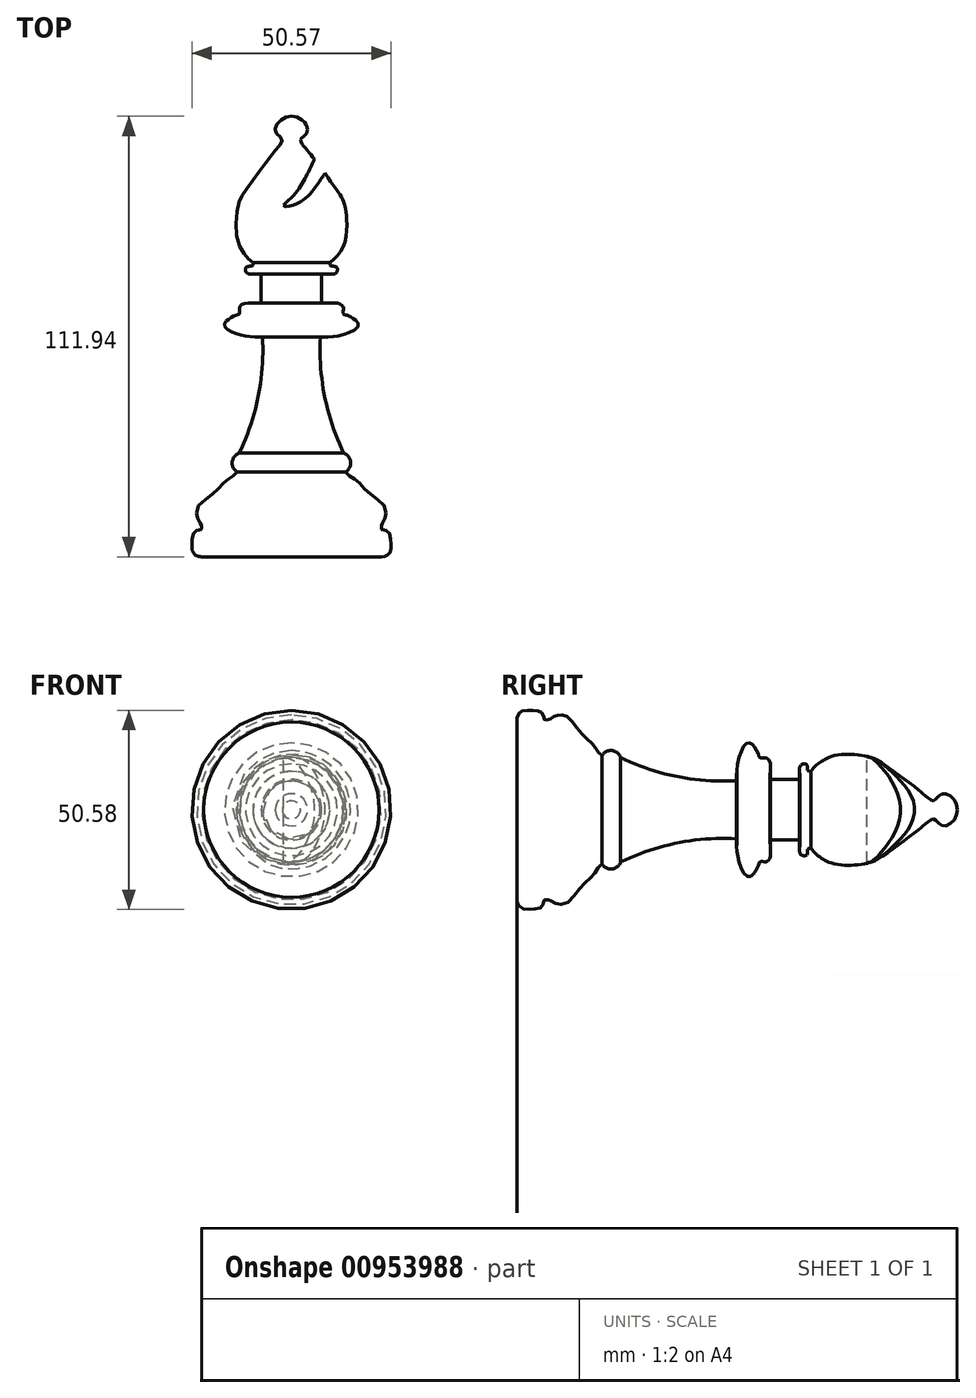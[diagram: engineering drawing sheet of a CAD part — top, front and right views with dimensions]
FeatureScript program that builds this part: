
annotation { "Feature Type Name" : "Feature", "Feature Type Description" : "" }
export const myFeature = defineFeature(function(context is Context, id is Id, definition is map)
    precondition{}
    {
        {
            var Q0;
            Q0=qCreatedBy(makeId("Top.planeOp"),FACE);
            var sketch = newSketch(context, id + "F0", { "sketchPlane" : qUnion([Q0])});
            skLineSegment(sketch, "E0", {"start": v(6.72, 66.6) * mm, "end": v(6.72, -45.31) * mm});
            skLineSegment(sketch, "E1", {"start": v(6.72, -45.31) * mm, "end": v(-15.55, -45.31) * mm});
            skFitSpline(sketch, "E2", {"points": [v(-15.55, -45.31) * mm, v(-16.6, -45.31) * mm, v(-18.04, -44.66) * mm, v(-18.53, -43.6) * mm, v(-18.53, -41.43) * mm, v(-18.4, -39.98) * mm, v(-17.92, -39.05) * mm, v(-16.91, -38.57) * mm, v(-16.19, -38.36) * mm, v(-16.1, -37.96) * mm, v(-16.19, -37.15) * mm, v(-16.75, -36.3) * mm, v(-17.12, -35.54) * mm, v(-17.32, -34.5) * mm, v(-17.16, -32.84) * mm, v(-14.45, -30.33) * mm, v(-11.67, -27.87) * mm, v(-9.7, -25.9) * mm, v(-8.08, -24.77) * mm, v(-7.07, -23.8) * mm], "startDerivative": vector(-21.72, -2.35) * mm, "endDerivative": vector(17.85, 19.31) * mm});
            skArc(sketch, "E3", {"start": v(-6.54, -19) * mm, "mid": v(-8.32, -21.23) * mm, "end": v(-7.07, -23.8) * mm});
            skArc(sketch, "E4", {"start": v(-6.54, -19) * mm, "mid": v(-1.72, -4.59) * mm, "end": v(-0.65, 10.57) * mm});
            skFitSpline(sketch, "E5", {"points": [v(-0.65, 10.57) * mm, v(-4.03, 10.57) * mm, v(-8.7, 11.9) * mm, v(-10.27, 13.25) * mm, v(-9.93, 14.4) * mm, v(-8.98, 15.15) * mm, v(-7.35, 16.04) * mm, v(-6.54, 16.3) * mm, v(-6.47, 17.32) * mm, v(-6.47, 18) * mm, v(-5.8, 18.82) * mm, v(-4.1, 19.09) * mm, v(-2.47, 18.95) * mm, v(-1.38, 18.96) * mm, v(-0.98, 19.04) * mm], "startDerivative": vector(-29.3, -2.17) * mm, "endDerivative": vector(9.52, 2.58) * mm});
            skLineSegment(sketch, "E6", {"start": v(-0.98, 19.04) * mm, "end": v(-0.98, 26.49) * mm});
            skFitSpline(sketch, "E7", {"points": [v(-0.98, 26.49) * mm, v(-2.7, 26.49) * mm, v(-4.03, 26.49) * mm, v(-4.7, 26.83) * mm, v(-4.94, 27.37) * mm, v(-4.7, 28.32) * mm, v(-3.41, 28.49) * mm, v(-3.08, 28.86) * mm, v(-3.08, 29.37) * mm], "startDerivative": vector(-10.25, 0.22) * mm, "endDerivative": vector(-0.6, 5.58) * mm});
            skFitSpline(sketch, "E8", {"points": [v(-3.08, 29.37) * mm, v(-4.8, 30.98) * mm, v(-7.1, 35.62) * mm, v(-6.74, 44.21) * mm, v(-5.24, 47.24) * mm, v(-0.98, 53.2) * mm, v(1.93, 57) * mm, v(3.83, 59.3) * mm, v(4.38, 60.66) * mm, v(3.3, 61.75) * mm, v(2.61, 63.1) * mm, v(3.16, 64.73) * mm, v(4.8, 66.11) * mm, v(6.72, 66.6) * mm], "startDerivative": vector(-25.3, 20.8) * mm, "endDerivative": vector(31.97, 4.82) * mm});
            skSolve(sketch);
        }
        {
            var Q0;
            Q0=makeQuery(id+"F0.imprint","IMPRINT",FACE,{"disambiguationData":[TD([[makeQuery(id+"F0.imprint","IMPRINT",EDGE,{"derivedFrom":sQuery(id+"F0.wireOp",EDGE,"E0")}),-1.0]])]});
            var Q1;
            Q1=sQuery(id+"F0.wireOp",EDGE,"E0");
            revolve(context, id + "F1", {"surfaceOperationType" : NewSurfaceOperationType.NEW, "entities" : qUnion([Q0]), "axis" : qUnion([Q1]), "revolveType" : RevolveType.FULL});
        }
        {
            var Q0;
            Q0=qCreatedBy(makeId("Top.planeOp"),FACE);
            cPlane(context, id + "F2", {"entities" : qUnion([Q0]), "cplaneType" : CPlaneType.OFFSET, "offset" : 56.64 * mm, "width" : 152.4 * mm, "height" : 152.4 * mm});
        }
        {
            var Q0;
            Q0=qCreatedBy(id+"F2.planeOp",FACE);
            var sketch = newSketch(context, id + "F3", { "sketchPlane" : qUnion([Q0])});
            skFitSpline(sketch, "E9", {"points": [v(12.7, 56.05) * mm, v(11.6, 53.61) * mm, v(9.7, 49.95) * mm, v(6.72, 45.88) * mm, v(4.68, 43.7) * mm, v(6.72, 43.84) * mm, v(10.65, 46.01) * mm, v(13.5, 49.54) * mm, v(15.27, 52.12) * mm], "startDerivative": vector(-9.24, -21.49) * mm, "endDerivative": vector(14.26, 20.84) * mm});
            skLineSegment(sketch, "E10", {"start": v(15.27, 52.12) * mm, "end": v(12.7, 56.05) * mm});
            skSolve(sketch);
        }
        {
            var Q0;
            Q0=makeQuery(id+"F3.imprint","IMPRINT",FACE,{"disambiguationData":[TD([[makeQuery(id+"F3.imprint","IMPRINT",EDGE,{"derivedFrom":sQuery(id+"F3.wireOp",EDGE,"E9")}),1.0]])]});
            extrude(context, id + "F4", {"entities" : qUnion([Q0]), "operationType" : NewBodyOperationType.REMOVE, "oppositeDirection" : true, "depth" : 99.57 * mm, "offsetDistance" : 25.4 * mm});
        }
    });
